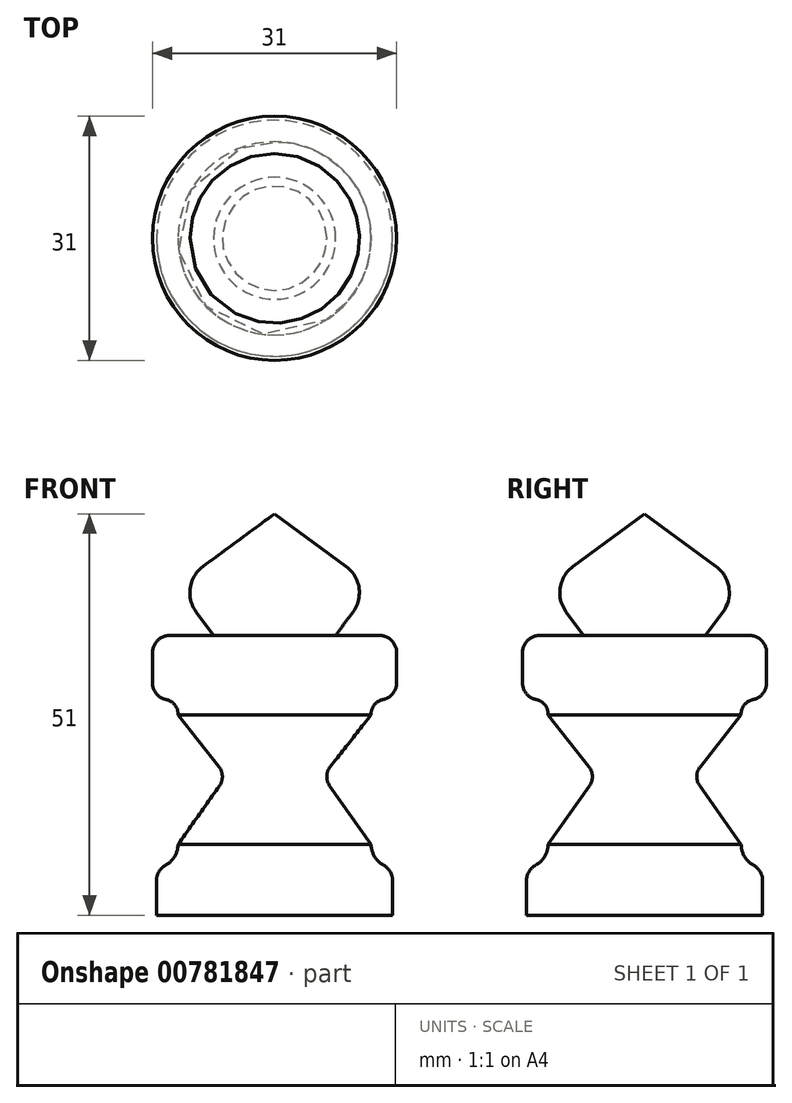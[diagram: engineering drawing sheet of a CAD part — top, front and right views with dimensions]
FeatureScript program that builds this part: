
annotation { "Feature Type Name" : "Feature", "Feature Type Description" : "" }
export const myFeature = defineFeature(function(context is Context, id is Id, definition is map)
    precondition{}
    {
        {
            var Q0;
            Q0=qCreatedBy(makeId("Front.planeOp"),FACE);
            var sketch = newSketch(context, id + "F0", { "sketchPlane" : qUnion([Q0])});
            skPoint(sketch, "E0.orphan", {"position": v(34, 39.81) * mm});
            skLineSegment(sketch, "E1.bottom", {"start": v(0, 0) * mm, "end": v(15, 0) * mm});
            skLineSegment(sketch, "E1.right", {"start": v(15, 0) * mm, "end": v(15, 6) * mm});
            skLineSegment(sketch, "E2.top", {"start": v(7.75, 35.54) * mm, "end": v(15.5, 35.54) * mm});
            skLineSegment(sketch, "E2.right", {"start": v(15.5, 28.33) * mm, "end": v(15.5, 35.54) * mm});
            skLineSegment(sketch, "E3", {"start": v(12.27, 25.46) * mm, "end": v(6.13, 17.68) * mm});
            skLineSegment(sketch, "E4", {"start": v(6.13, 17.68) * mm, "end": v(12.27, 9) * mm});
            skPoint(sketch, "E5.orphan", {"position": v(12.27, 17.68) * mm});
            skArc(sketch, "E6", {"start": v(14.12, 27.43) * mm, "mid": v(12.77, 26.84) * mm, "end": v(12.27, 25.46) * mm});
            skArc(sketch, "E7", {"start": v(12.27, 9) * mm, "mid": v(13.05, 6.97) * mm, "end": v(15, 6) * mm});
            skArc(sketch, "E8", {"start": v(14.12, 27.43) * mm, "mid": v(14.94, 27.67) * mm, "end": v(15.5, 28.33) * mm});
            skLineSegment(sketch, "E9", {"start": v(0, 51) * mm, "end": v(12.4, 41.87) * mm});
            skLineSegment(sketch, "E10", {"start": v(12.4, 41.87) * mm, "end": v(7.75, 35.54) * mm});
            skPoint(sketch, "E11.orphan", {"position": v(9.3, 48.2) * mm});
            skLineSegment(sketch, "E12", {"start": v(0, 51) * mm, "end": v(0, 0) * mm});
            skSolve(sketch);
        }
        {
            var Q0;
            Q0=makeQuery(id+"F0.imprint","IMPRINT",FACE,{"disambiguationData":[TD([[makeQuery(id+"F0.imprint","IMPRINT",EDGE,{"derivedFrom":sQuery(id+"F0.wireOp",EDGE,"E1.bottom")}),1.0]])]});
            var Q1;
            Q1=sQuery(id+"F0.wireOp",EDGE,"E12");
            revolve(context, id + "F1", {"surfaceOperationType" : NewSurfaceOperationType.NEW, "entities" : qUnion([Q0]), "axis" : qUnion([Q1]), "revolveType" : RevolveType.FULL});
        }
        {
            var Q0;
            Q0=makeQuery(id+"F1.opRevolve","SWEPT_EDGE",EDGE,{"disambiguationData":[OSD([sQuery(id+"F0.wireOp",EDGE,"E2.right"),sQuery(id+"F0.wireOp",EDGE,"E2.top")])]});
            fillet(context, id + "F2", {"entities" : qUnion([Q0]), "radius" : 2.17 * mm, "tangentPropagation" : true, "allowEdgeOverflow" : false});
        }
        {
            var Q0;
            Q0=makeQuery(id+"F1.opRevolve","SWEPT_EDGE",EDGE,{"disambiguationData":[OSD([sQuery(id+"F0.wireOp",EDGE,"E3"),sQuery(id+"F0.wireOp",EDGE,"E4")])]});
            fillet(context, id + "F3", {"entities" : qUnion([Q0]), "radius" : 2.02 * mm, "tangentPropagation" : true, "allowEdgeOverflow" : false});
        }
        {
            var Q0;
            Q0=makeQuery(id+"F1.opRevolve","SWEPT_EDGE",EDGE,{"disambiguationData":[OSD([sQuery(id+"F0.wireOp",EDGE,"E1.right"),sQuery(id+"F0.wireOp",EDGE,"E7")])]});
            fillet(context, id + "F4", {"entities" : qUnion([Q0]), "radius" : 2.27 * mm, "tangentPropagation" : true, "allowEdgeOverflow" : false});
        }
        {
            var Q0;
            Q0=makeQuery(id+"F1.opRevolve","SWEPT_EDGE",EDGE,{"disambiguationData":[OSD([sQuery(id+"F0.wireOp",EDGE,"E9"),sQuery(id+"F0.wireOp",EDGE,"E10")])]});
            fillet(context, id + "F5", {"entities" : qUnion([Q0]), "radius" : 4.11 * mm, "tangentPropagation" : true, "allowEdgeOverflow" : false});
        }
    });
